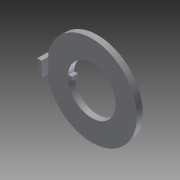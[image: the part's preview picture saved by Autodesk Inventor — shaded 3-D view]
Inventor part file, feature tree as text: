
AUTODESK INVENTOR PART (.ipt)
format: ipt  version: 2011 SP1 (Build 150282100, 282)  size: 96,768 bytes
history: native  units: in
note: dims shown in document units (in); Inventor stores cm internally (conversion verified against a paired STEP export)
features: other x7, extrude x2, sketch x2
ambient origin geometry x8: Origin, YZ Plane, XZ Plane, XY Plane, X Axis, Y Axis, Z Axis, Center Point
bodies: Solid1 (feature_tree)
feature tree (11):
  extrude  "Extrusion1"  Depth=0.079in TaperAngle=0.0deg
  extrude  "Extrusion2"  [1 undecoded]
  other  "ring_XY"
  other  "ring_YZ"
  other  "ring_ZX"
  other  "ring_X"
  other  "ring_Y"
  other  "ring_Z"
  other  "ring_Center"
  sketch  "Sketch_4"
  sketch  "Sketch_2"  dims[d0=0.031in d1=0.0in d2=0.079in d3=0.0in]
note: 1 required parameter value undecoded (feature->parameter linkage not recoverable at this tier; creation-order binding heuristic only, values carry confidence <= 0.55)
